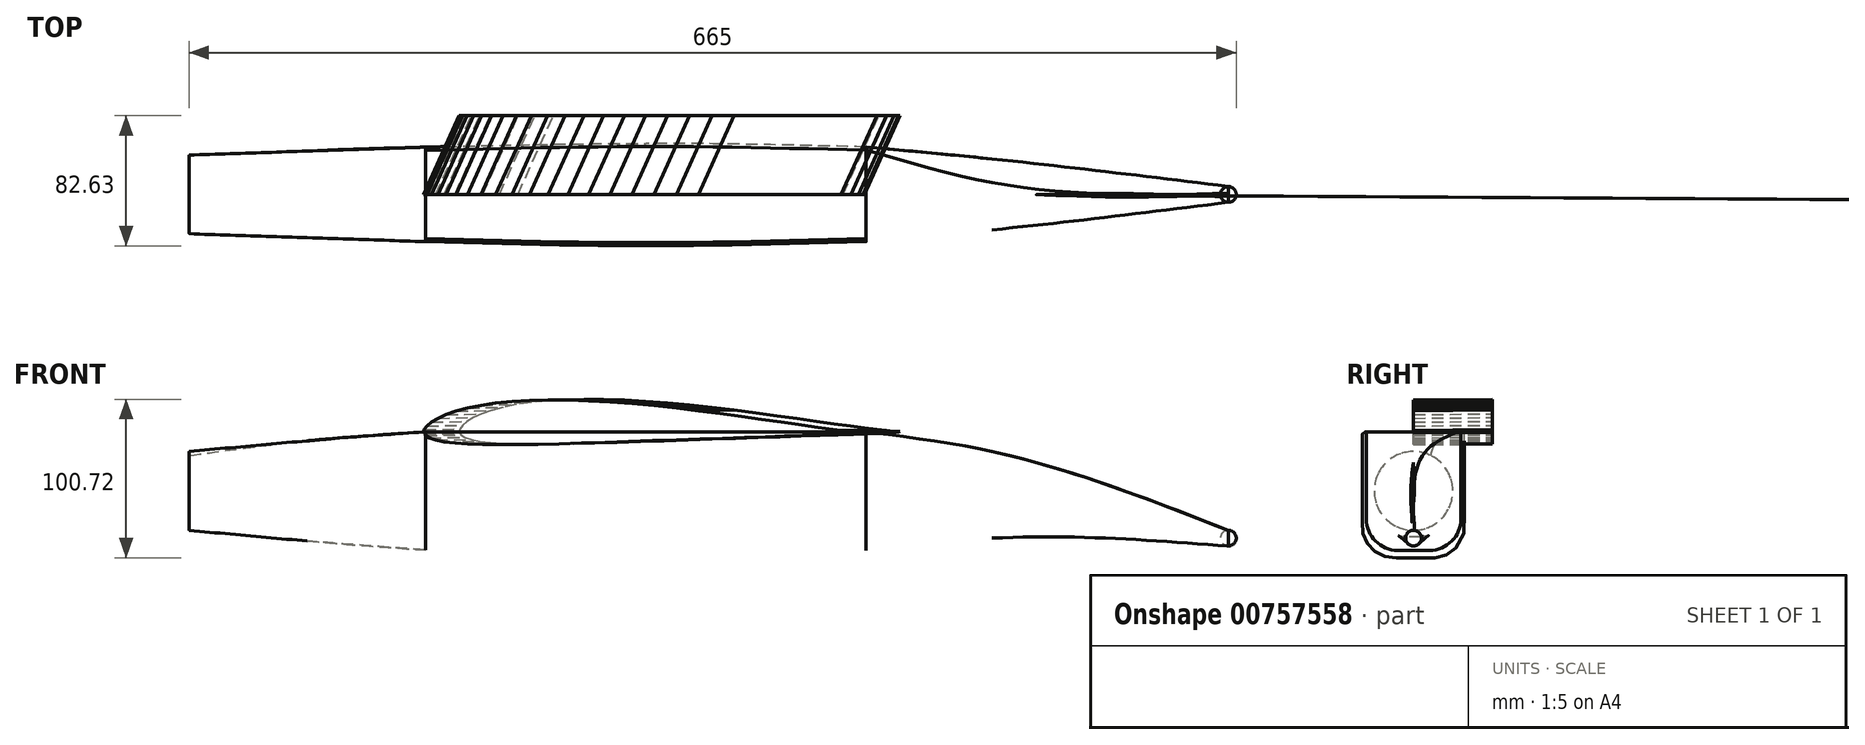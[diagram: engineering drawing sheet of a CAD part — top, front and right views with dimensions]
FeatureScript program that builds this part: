
annotation { "Feature Type Name" : "Feature", "Feature Type Description" : "" }
export const myFeature = defineFeature(function(context is Context, id is Id, definition is map)
    precondition{}
    {
        {
            var Q0;
            Q0=qCreatedBy(makeId("Right.planeOp"),FACE);
            cPlane(context, id + "F0", {"entities" : qUnion([Q0]), "cplaneType" : CPlaneType.OFFSET, "offset" : 150 * mm, "oppositeDirection" : true, "width" : 150 * mm, "height" : 150 * mm});
        }
        {
            var Q0;
            Q0=qCreatedBy(makeId("Right.planeOp"),FACE);
            cPlane(context, id + "F1", {"entities" : qUnion([Q0]), "cplaneType" : CPlaneType.OFFSET, "offset" : 280 * mm, "width" : 150 * mm, "height" : 150 * mm});
        }
        {
            var Q0;
            Q0=qCreatedBy(id+"F1.planeOp",FACE);
            cPlane(context, id + "F2", {"entities" : qUnion([Q0]), "cplaneType" : CPlaneType.OFFSET, "offset" : 230 * mm, "width" : 150 * mm, "height" : 150 * mm});
        }
        {
            var Q0;
            Q0=qCreatedBy(id+"F0.planeOp",FACE);
            var sketch = newSketch(context, id + "F3", { "sketchPlane" : qUnion([Q0])});
            skCircle(sketch, "E0", {"center": v(0, 0) * mm, "radius": 25 * mm});
            skSolve(sketch);
        }
        {
            var Q0;
            Q0=qCreatedBy(makeId("Right.planeOp"),FACE);
            var sketch = newSketch(context, id + "F4", { "sketchPlane" : qUnion([Q0])});
            skLineSegment(sketch, "E1.bottom", {"start": v(10, -37.5) * mm, "end": v(-10, -37.5) * mm});
            skLineSegment(sketch, "E1.top", {"start": v(28, 37.5) * mm, "end": v(-28, 37.5) * mm});
            skLineSegment(sketch, "E1.left", {"start": v(30, -17.5) * mm, "end": v(30, 35.5) * mm});
            skLineSegment(sketch, "E1.right", {"start": v(-30, -17.5) * mm, "end": v(-30, 35.5) * mm});
            skPoint(sketch, "E2.visualSharp", {"position": v(30, 37.5) * mm});
            skArc(sketch, "E2.filletArc", {"start": v(30, 35.5) * mm, "mid": v(29.41, 36.91) * mm, "end": v(28, 37.5) * mm});
            skPoint(sketch, "E3.visualSharp", {"position": v(-30, 37.5) * mm});
            skArc(sketch, "E3.filletArc", {"start": v(-28, 37.5) * mm, "mid": v(-29.41, 36.91) * mm, "end": v(-30, 35.5) * mm});
            skPoint(sketch, "E4.visualSharp", {"position": v(30, -37.5) * mm});
            skArc(sketch, "E4.filletArc", {"start": v(10, -37.5) * mm, "mid": v(24.14, -31.64) * mm, "end": v(30, -17.5) * mm});
            skPoint(sketch, "E5.visualSharp", {"position": v(-30, -37.5) * mm});
            skArc(sketch, "E5.filletArc", {"start": v(-30, -17.5) * mm, "mid": v(-24.14, -31.64) * mm, "end": v(-10, -37.5) * mm});
            skSolve(sketch);
        }
        {
            var Q0;
            Q0=qCreatedBy(id+"F1.planeOp",FACE);
            var sketch = newSketch(context, id + "F5", { "sketchPlane" : qUnion([Q0])});
            skLineSegment(sketch, "E6.bottom", {"start": v(28.14, 37.5) * mm, "end": v(-28, 37.5) * mm});
            skLineSegment(sketch, "E6.top", {"start": v(10.14, -37.77) * mm, "end": v(-10, -37.77) * mm});
            skLineSegment(sketch, "E6.left", {"start": v(30.14, 35.5) * mm, "end": v(30.14, -17.77) * mm});
            skLineSegment(sketch, "E6.right", {"start": v(-30, 35.5) * mm, "end": v(-30, -17.77) * mm});
            skPoint(sketch, "E7.visualSharp", {"position": v(30.14, -37.77) * mm});
            skArc(sketch, "E7.filletArc", {"start": v(10.14, -37.77) * mm, "mid": v(24.28, -31.9) * mm, "end": v(30.14, -17.77) * mm});
            skPoint(sketch, "E8.visualSharp", {"position": v(-30, -37.77) * mm});
            skArc(sketch, "E8.filletArc", {"start": v(-30, -17.77) * mm, "mid": v(-24.14, -31.9) * mm, "end": v(-10, -37.77) * mm});
            skPoint(sketch, "E9.visualSharp", {"position": v(30.14, 37.5) * mm});
            skArc(sketch, "E9.filletArc", {"start": v(30.14, 35.5) * mm, "mid": v(29.56, 36.91) * mm, "end": v(28.14, 37.5) * mm});
            skPoint(sketch, "E10.visualSharp", {"position": v(-30, 37.5) * mm});
            skArc(sketch, "E10.filletArc", {"start": v(-28, 37.5) * mm, "mid": v(-29.41, 36.91) * mm, "end": v(-30, 35.5) * mm});
            skSolve(sketch);
        }
        {
            var Q0;
            Q0=qCreatedBy(id+"F2.planeOp",FACE);
            var sketch = newSketch(context, id + "F6", { "sketchPlane" : qUnion([Q0])});
            skCircle(sketch, "E11", {"center": v(0, -30) * mm, "radius": 5 * mm});
            skSolve(sketch);
        }
        {
            var Q0;
            Q0=qCreatedBy(makeId("Right.planeOp"),FACE);
            cPlane(context, id + "F7", {"entities" : qUnion([Q0]), "cplaneType" : CPlaneType.OFFSET, "offset" : 75 * mm, "oppositeDirection" : true, "width" : 150 * mm, "height" : 150 * mm});
        }
        {
            var Q0;
            Q0=qCreatedBy(makeId("Right.planeOp"),FACE);
            cPlane(context, id + "F8", {"entities" : qUnion([Q0]), "cplaneType" : CPlaneType.OFFSET, "offset" : 140 * mm, "width" : 150 * mm, "height" : 150 * mm});
        }
        {
            var Q0;
            Q0=qCreatedBy(id+"F1.planeOp",FACE);
            cPlane(context, id + "F9", {"entities" : qUnion([Q0]), "cplaneType" : CPlaneType.OFFSET, "offset" : 80 * mm, "width" : 150 * mm, "height" : 150 * mm});
        }
        {
            var Q0;
            Q0=qCreatedBy(id+"F7.planeOp",FACE);
            var sketch = newSketch(context, id + "F10", { "sketchPlane" : qUnion([Q0])});
            skLineSegment(sketch, "E12.bottom", {"start": v(15.5, 31.79) * mm, "end": v(-15.5, 31.79) * mm});
            skLineSegment(sketch, "E12.top", {"start": v(5.5, -31.78) * mm, "end": v(-5.5, -31.78) * mm});
            skLineSegment(sketch, "E12.left", {"start": v(27.5, 19.79) * mm, "end": v(27.5, -9.78) * mm});
            skLineSegment(sketch, "E12.right", {"start": v(-27.5, 19.79) * mm, "end": v(-27.5, -9.78) * mm});
            skPoint(sketch, "E13.visualSharp", {"position": v(27.5, -31.78) * mm});
            skArc(sketch, "E13.filletArc", {"start": v(5.5, -31.78) * mm, "mid": v(21.06, -25.33) * mm, "end": v(27.5, -9.78) * mm});
            skPoint(sketch, "E14.visualSharp", {"position": v(-27.5, -31.78) * mm});
            skArc(sketch, "E14.filletArc", {"start": v(-27.5, -9.78) * mm, "mid": v(-21.06, -25.33) * mm, "end": v(-5.5, -31.78) * mm});
            skPoint(sketch, "E15.visualSharp", {"position": v(27.5, 31.79) * mm});
            skArc(sketch, "E15.filletArc", {"start": v(27.5, 19.79) * mm, "mid": v(23.99, 28.28) * mm, "end": v(15.5, 31.79) * mm});
            skPoint(sketch, "E16.visualSharp", {"position": v(-27.5, 31.79) * mm});
            skArc(sketch, "E16.filletArc", {"start": v(-15.5, 31.79) * mm, "mid": v(-23.99, 28.28) * mm, "end": v(-27.5, 19.79) * mm});
            skSolve(sketch);
        }
        {
            var Q0;
            Q0=qCreatedBy(id+"F8.planeOp",FACE);
            var sketch = newSketch(context, id + "F11", { "sketchPlane" : qUnion([Q0])});
            skLineSegment(sketch, "E17.bottom", {"start": v(30.37, 37.5) * mm, "end": v(-30.63, 37.5) * mm});
            skLineSegment(sketch, "E17.top", {"start": v(12.37, -42.5) * mm, "end": v(-12.63, -42.5) * mm});
            skLineSegment(sketch, "E17.left", {"start": v(32.37, 35.5) * mm, "end": v(32.37, -22.5) * mm});
            skLineSegment(sketch, "E17.right", {"start": v(-32.63, 35.5) * mm, "end": v(-32.63, -22.5) * mm});
            skPoint(sketch, "E18.visualSharp", {"position": v(32.37, -42.5) * mm});
            skArc(sketch, "E18.filletArc", {"start": v(12.37, -42.5) * mm, "mid": v(26.52, -36.64) * mm, "end": v(32.37, -22.5) * mm});
            skPoint(sketch, "E19.visualSharp", {"position": v(-32.63, -42.5) * mm});
            skArc(sketch, "E19.filletArc", {"start": v(-32.63, -22.5) * mm, "mid": v(-26.77, -36.64) * mm, "end": v(-12.63, -42.5) * mm});
            skPoint(sketch, "E20.visualSharp", {"position": v(32.37, 37.5) * mm});
            skArc(sketch, "E20.filletArc", {"start": v(32.37, 35.5) * mm, "mid": v(31.79, 36.91) * mm, "end": v(30.37, 37.5) * mm});
            skPoint(sketch, "E21.visualSharp", {"position": v(-32.63, 37.5) * mm});
            skArc(sketch, "E21.filletArc", {"start": v(-30.63, 37.5) * mm, "mid": v(-32.04, 36.91) * mm, "end": v(-32.63, 35.5) * mm});
            skSolve(sketch);
        }
        {
            var Q0;
            Q0=makeQuery(id+"F3.imprint","IMPRINT",FACE,{"disambiguationData":[TD([[makeQuery(id+"F3.imprint","IMPRINT",EDGE,{"derivedFrom":sQuery(id+"F3.wireOp",EDGE,"E0")}),1.0]])]});
            var Q1;
            Q1=makeQuery(id+"F10.imprint","IMPRINT",FACE,{"disambiguationData":[TD([[makeQuery(id+"F10.imprint","IMPRINT",EDGE,{"derivedFrom":sQuery(id+"F10.wireOp",EDGE,"E12.bottom")}),1.0]])]});
            var Q2;
            Q2=makeQuery(id+"F4.imprint","IMPRINT",FACE,{"disambiguationData":[TD([[makeQuery(id+"F4.imprint","IMPRINT",EDGE,{"derivedFrom":sQuery(id+"F4.wireOp",EDGE,"E1.bottom")}),-1.0]])]});
            loft(context, id + "F12", {"sheetProfilesArray" : [{ "sheetProfileEntities" : qUnion([Q0]) }, { "sheetProfileEntities" : qUnion([Q1]) }, { "sheetProfileEntities" : qUnion([Q2]) }]});
        }
        {
            var Q0;
            Q0=qCreatedBy(id+"F9.planeOp",FACE);
            var sketch = newSketch(context, id + "F13", { "sketchPlane" : qUnion([Q0])});
            skLineSegment(sketch, "E22.bottom", {"start": v(-7.5, 25) * mm, "end": v(7.5, 25) * mm});
            skLineSegment(sketch, "E22.top", {"start": v(-7.5, -30) * mm, "end": v(7.5, -30) * mm});
            skLineSegment(sketch, "E22.left", {"start": v(-22.5, 10) * mm, "end": v(-22.5, -15) * mm});
            skLineSegment(sketch, "E22.right", {"start": v(22.5, 10) * mm, "end": v(22.5, -15) * mm});
            skPoint(sketch, "E23.visualSharp", {"position": v(-22.5, 25) * mm});
            skArc(sketch, "E23.filletArc", {"start": v(-7.5, 25) * mm, "mid": v(-18.1, 20.6) * mm, "end": v(-22.5, 10) * mm});
            skPoint(sketch, "E24.visualSharp", {"position": v(22.5, 25) * mm});
            skArc(sketch, "E24.filletArc", {"start": v(22.5, 10) * mm, "mid": v(18.1, 20.6) * mm, "end": v(7.5, 25) * mm});
            skPoint(sketch, "E25.visualSharp", {"position": v(22.5, -30) * mm});
            skArc(sketch, "E25.filletArc", {"start": v(7.5, -30) * mm, "mid": v(18.1, -25.6) * mm, "end": v(22.5, -15) * mm});
            skPoint(sketch, "E26.visualSharp", {"position": v(-22.5, -30) * mm});
            skArc(sketch, "E26.filletArc", {"start": v(-22.5, -15) * mm, "mid": v(-18.1, -25.6) * mm, "end": v(-7.5, -30) * mm});
            skSolve(sketch);
        }
        {
            var Q0;
            Q0=makeQuery(id+"F5.imprint","IMPRINT",FACE,{"disambiguationData":[TD([[makeQuery(id+"F5.imprint","IMPRINT",EDGE,{"derivedFrom":sQuery(id+"F5.wireOp",EDGE,"E6.bottom")}),1.0]])]});
            var Q1;
            Q1=makeQuery(id+"F13.imprint","IMPRINT",FACE,{"disambiguationData":[TD([[makeQuery(id+"F13.imprint","IMPRINT",EDGE,{"derivedFrom":sQuery(id+"F13.wireOp",EDGE,"E22.bottom")}),-1.0]])]});
            var Q2;
            Q2=makeQuery(id+"F6.imprint","IMPRINT",FACE,{"disambiguationData":[TD([[makeQuery(id+"F6.imprint","IMPRINT",EDGE,{"derivedFrom":sQuery(id+"F6.wireOp",EDGE,"E11")}),1.0]])]});
            loft(context, id + "F14", {"sheetProfilesArray" : [{ "sheetProfileEntities" : qUnion([Q0]) }, { "sheetProfileEntities" : qUnion([Q1]) }, { "sheetProfileEntities" : qUnion([Q2]) }]});
        }
        {
            var Q0;
            Q0=makeQuery(id+"F12.opLoft","CAP_FACE",FACE,{"disambiguationData":[OSD([makeQuery(id+"F4.imprint","IMPRINT",FACE,{"disambiguationData":[TD([[makeQuery(id+"F4.imprint","IMPRINT",EDGE,{"derivedFrom":sQuery(id+"F4.wireOp",EDGE,"E1.bottom")}),-1.0]])]})])],"isStart":true});
            var Q1;
            Q1=makeQuery(id+"F11.imprint","IMPRINT",FACE,{"disambiguationData":[TD([[makeQuery(id+"F11.imprint","IMPRINT",EDGE,{"derivedFrom":sQuery(id+"F11.wireOp",EDGE,"E17.bottom")}),1.0]])]});
            var Q2;
            Q2=makeQuery(id+"F14.opLoft","CAP_FACE",FACE,{"disambiguationData":[OSD([makeQuery(id+"F5.imprint","IMPRINT",FACE,{"disambiguationData":[TD([[makeQuery(id+"F5.imprint","IMPRINT",EDGE,{"derivedFrom":sQuery(id+"F5.wireOp",EDGE,"E6.bottom")}),1.0]])]})])],"isStart":true});
            loft(context, id + "F15", {"sheetProfilesArray" : [{ "sheetProfileEntities" : qUnion([Q0]) }, { "sheetProfileEntities" : qUnion([Q1]) }, { "sheetProfileEntities" : qUnion([Q2]) }]});
        }
        {
            var Q0;
            Q0=qCreatedBy(id+"F2.planeOp",FACE);
            var sketch = newSketch(context, id + "F16", { "sketchPlane" : qUnion([Q0])});
            skCircle(sketch, "E27", {"center": v(0, -30) * mm, "radius": 5 * mm});
            skLineSegment(sketch, "E28", {"start": v(0, -45) * mm, "end": v(0, -15) * mm});
            skSolve(sketch);
        }
        {
            var Q0;
            {var subQ0=sQuery(id+"F16.wireOp",EDGE,"E28");var subQ1=sQuery(id+"F16.wireOp",EDGE,"E27");var subQ2=makeQuery(id+"F16.imprint","INTERSECT",VERTEX,{"disambiguationData":[OD(0.0)],"derivedFrom":[subQ1,subQ0]});Q0=makeQuery(id+"F16.imprint","IMPRINT",FACE,{"disambiguationData":[TD([[makeQuery(id+"F16.imprint","IMPRINT",EDGE,{"disambiguationData":[TD([[subQ2,1.0]])],"derivedFrom":subQ1}),1.0]])]});}
            var Q1;
            Q1=sQuery(id+"F16.wireOp",EDGE,"E27");
            var Q2;
            Q2=sQuery(id+"F16.wireOp",EDGE,"E28");
            revolve(context, id + "F17", {"surfaceOperationType" : NewSurfaceOperationType.NEW, "entities" : qUnion([Q0]), "surfaceEntities" : qUnion([Q1]), "axis" : qUnion([Q2]), "revolveType" : RevolveType.FULL});
        }
        {
            var Q0;
            Q0=qCreatedBy(makeId("Front.planeOp"),FACE);
            cPlane(context, id + "F18", {"entities" : qUnion([Q0]), "cplaneType" : CPlaneType.OFFSET, "offset" : 50 * mm, "width" : 150 * mm, "height" : 150 * mm});
        }
        {
            var Q0;
            Q0=qCreatedBy(makeId("Front.planeOp"),FACE);
            cPlane(context, id + "F19", {"entities" : qUnion([Q0]), "cplaneType" : CPlaneType.OFFSET, "offset" : 50 * mm, "oppositeDirection" : true, "width" : 150 * mm, "height" : 150 * mm});
        }
        {
            var Q0;
            Q0=qCreatedBy(makeId("Front.planeOp"),FACE);
            var sketch = newSketch(context, id + "F20", { "sketchPlane" : qUnion([Q0])});
            skLineSegment(sketch, "E29", {"start": v(278.84, 37.19) * mm, "end": v(277.87, 37.23) * mm});
            skLineSegment(sketch, "E30", {"start": v(277.87, 37.23) * mm, "end": v(275, 37.41) * mm});
            skLineSegment(sketch, "E31", {"start": v(275, 37.41) * mm, "end": v(270.35, 37.84) * mm});
            skLineSegment(sketch, "E32", {"start": v(270.35, 37.84) * mm, "end": v(264.1, 38.54) * mm});
            skLineSegment(sketch, "E33", {"start": v(264.1, 38.54) * mm, "end": v(256.35, 39.5) * mm});
            skLineSegment(sketch, "E34", {"start": v(256.35, 39.5) * mm, "end": v(247.27, 40.72) * mm});
            skLineSegment(sketch, "E35", {"start": v(247.27, 40.72) * mm, "end": v(237.01, 42.16) * mm});
            skLineSegment(sketch, "E36", {"start": v(237.01, 42.16) * mm, "end": v(225.73, 43.77) * mm});
            skLineSegment(sketch, "E37", {"start": v(225.73, 43.77) * mm, "end": v(213.58, 45.5) * mm});
            skLineSegment(sketch, "E38", {"start": v(213.58, 45.5) * mm, "end": v(200.7, 47.32) * mm});
            skLineSegment(sketch, "E39", {"start": v(200.7, 47.32) * mm, "end": v(187.3, 49.14) * mm});
            skLineSegment(sketch, "E40", {"start": v(187.3, 49.14) * mm, "end": v(173.48, 50.93) * mm});
            skLineSegment(sketch, "E41", {"start": v(173.48, 50.93) * mm, "end": v(159.43, 52.62) * mm});
            skLineSegment(sketch, "E42", {"start": v(159.43, 52.62) * mm, "end": v(145.3, 54.14) * mm});
            skLineSegment(sketch, "E43", {"start": v(145.3, 54.14) * mm, "end": v(131.22, 55.46) * mm});
            skLineSegment(sketch, "E44", {"start": v(131.22, 55.46) * mm, "end": v(117.33, 56.52) * mm});
            skLineSegment(sketch, "E45", {"start": v(117.33, 56.52) * mm, "end": v(103.77, 57.28) * mm});
            skLineSegment(sketch, "E46", {"start": v(103.77, 57.28) * mm, "end": v(90.65, 57.71) * mm});
            skLineSegment(sketch, "E47", {"start": v(90.65, 57.71) * mm, "end": v(78.09, 57.8) * mm});
            skLineSegment(sketch, "E48", {"start": v(78.09, 57.8) * mm, "end": v(66.2, 57.5) * mm});
            skLineSegment(sketch, "E49", {"start": v(66.2, 57.5) * mm, "end": v(55.05, 56.83) * mm});
            skLineSegment(sketch, "E50", {"start": v(55.05, 56.83) * mm, "end": v(44.74, 55.79) * mm});
            skLineSegment(sketch, "E51", {"start": v(44.74, 55.79) * mm, "end": v(35.34, 54.39) * mm});
            skLineSegment(sketch, "E52", {"start": v(35.34, 54.39) * mm, "end": v(26.9, 52.67) * mm});
            skLineSegment(sketch, "E53", {"start": v(26.9, 52.67) * mm, "end": v(19.5, 50.68) * mm});
            skLineSegment(sketch, "E54", {"start": v(19.5, 50.68) * mm, "end": v(13.15, 48.48) * mm});
            skLineSegment(sketch, "E55", {"start": v(13.15, 48.48) * mm, "end": v(7.93, 46.13) * mm});
            skLineSegment(sketch, "E56", {"start": v(7.93, 46.13) * mm, "end": v(3.87, 43.7) * mm});
            skLineSegment(sketch, "E57", {"start": v(3.87, 43.7) * mm, "end": v(1, 41.27) * mm});
            skLineSegment(sketch, "E58", {"start": v(1, 41.27) * mm, "end": v(-0.68, 38.93) * mm});
            skLineSegment(sketch, "E59", {"start": v(-0.68, 38.93) * mm, "end": v(-1.1, 37.72) * mm});
            skLineSegment(sketch, "E60", {"start": v(-1.1, 37.72) * mm, "end": v(-1.16, 37.22) * mm});
            skLineSegment(sketch, "E61", {"start": v(-1.16, 37.22) * mm, "end": v(-1.11, 36.78) * mm});
            skLineSegment(sketch, "E62", {"start": v(-1.11, 36.78) * mm, "end": v(-0.96, 36.36) * mm});
            skLineSegment(sketch, "E63", {"start": v(-0.96, 36.36) * mm, "end": v(-0.69, 35.94) * mm});
            skLineSegment(sketch, "E64", {"start": v(-0.69, 35.94) * mm, "end": v(0, 35.22) * mm});
            skLineSegment(sketch, "E65", {"start": v(0, 35.22) * mm, "end": v(2.6, 33.63) * mm});
            skLineSegment(sketch, "E66", {"start": v(2.6, 33.63) * mm, "end": v(6.61, 32.26) * mm});
            skLineSegment(sketch, "E67", {"start": v(6.61, 32.26) * mm, "end": v(12, 31.15) * mm});
            skLineSegment(sketch, "E68", {"start": v(12, 31.15) * mm, "end": v(18.78, 30.33) * mm});
            skLineSegment(sketch, "E69", {"start": v(18.78, 30.33) * mm, "end": v(26.93, 29.78) * mm});
            skLineSegment(sketch, "E70", {"start": v(26.93, 29.78) * mm, "end": v(36.36, 29.46) * mm});
            skLineSegment(sketch, "E71", {"start": v(36.36, 29.46) * mm, "end": v(47, 29.36) * mm});
            skLineSegment(sketch, "E72", {"start": v(47, 29.36) * mm, "end": v(58.76, 29.43) * mm});
            skLineSegment(sketch, "E73", {"start": v(58.76, 29.43) * mm, "end": v(71.48, 29.64) * mm});
            skLineSegment(sketch, "E74", {"start": v(71.48, 29.64) * mm, "end": v(85.03, 29.98) * mm});
            skLineSegment(sketch, "E75", {"start": v(85.03, 29.98) * mm, "end": v(99.25, 30.4) * mm});
            skLineSegment(sketch, "E76", {"start": v(99.25, 30.4) * mm, "end": v(113.98, 30.87) * mm});
            skLineSegment(sketch, "E77", {"start": v(113.98, 30.87) * mm, "end": v(129.03, 31.38) * mm});
            skLineSegment(sketch, "E78", {"start": v(129.03, 31.38) * mm, "end": v(144.22, 31.92) * mm});
            skLineSegment(sketch, "E79", {"start": v(144.22, 31.92) * mm, "end": v(159.37, 32.45) * mm});
            skLineSegment(sketch, "E80", {"start": v(159.37, 32.45) * mm, "end": v(174.3, 32.97) * mm});
            skLineSegment(sketch, "E81", {"start": v(174.3, 32.97) * mm, "end": v(188.81, 33.48) * mm});
            skLineSegment(sketch, "E82", {"start": v(188.81, 33.48) * mm, "end": v(202.75, 33.95) * mm});
            skLineSegment(sketch, "E83", {"start": v(202.75, 33.95) * mm, "end": v(215.93, 34.4) * mm});
            skLineSegment(sketch, "E84", {"start": v(215.93, 34.4) * mm, "end": v(228.2, 34.82) * mm});
            skLineSegment(sketch, "E85", {"start": v(228.2, 34.82) * mm, "end": v(239.41, 35.2) * mm});
            skLineSegment(sketch, "E86", {"start": v(239.41, 35.2) * mm, "end": v(249.42, 35.54) * mm});
            skLineSegment(sketch, "E87", {"start": v(249.42, 35.54) * mm, "end": v(258.1, 35.87) * mm});
            skLineSegment(sketch, "E88", {"start": v(258.1, 35.87) * mm, "end": v(265.36, 36.18) * mm});
            skLineSegment(sketch, "E89", {"start": v(265.36, 36.18) * mm, "end": v(271.1, 36.48) * mm});
            skLineSegment(sketch, "E90", {"start": v(271.1, 36.48) * mm, "end": v(275.28, 36.8) * mm});
            skLineSegment(sketch, "E91", {"start": v(275.28, 36.8) * mm, "end": v(277.91, 37.08) * mm});
            skLineSegment(sketch, "E92", {"start": v(277.91, 37.08) * mm, "end": v(278.84, 37.19) * mm});
            skSolve(sketch);
        }
        {
            var Q0;
            Q0=qCreatedBy(id+"F18.planeOp",FACE);
            var sketch = newSketch(context, id + "F21", { "sketchPlane" : qUnion([Q0])});
            skLineSegment(sketch, "E93", {"start": v(301.34, 37.61) * mm, "end": v(300.37, 37.65) * mm});
            skLineSegment(sketch, "E94", {"start": v(300.37, 37.65) * mm, "end": v(297.5, 37.84) * mm});
            skLineSegment(sketch, "E95", {"start": v(297.5, 37.84) * mm, "end": v(292.85, 38.27) * mm});
            skLineSegment(sketch, "E96", {"start": v(292.85, 38.27) * mm, "end": v(286.6, 38.96) * mm});
            skLineSegment(sketch, "E97", {"start": v(286.6, 38.96) * mm, "end": v(278.85, 39.93) * mm});
            skLineSegment(sketch, "E98", {"start": v(278.85, 39.93) * mm, "end": v(269.77, 41.15) * mm});
            skLineSegment(sketch, "E99", {"start": v(269.77, 41.15) * mm, "end": v(259.51, 42.58) * mm});
            skLineSegment(sketch, "E100", {"start": v(259.51, 42.58) * mm, "end": v(248.23, 44.2) * mm});
            skLineSegment(sketch, "E101", {"start": v(248.23, 44.2) * mm, "end": v(236.08, 45.93) * mm});
            skLineSegment(sketch, "E102", {"start": v(236.08, 45.93) * mm, "end": v(223.2, 47.74) * mm});
            skLineSegment(sketch, "E103", {"start": v(223.2, 47.74) * mm, "end": v(209.8, 49.57) * mm});
            skLineSegment(sketch, "E104", {"start": v(209.8, 49.57) * mm, "end": v(195.98, 51.36) * mm});
            skLineSegment(sketch, "E105", {"start": v(195.98, 51.36) * mm, "end": v(181.93, 53.04) * mm});
            skLineSegment(sketch, "E106", {"start": v(181.93, 53.04) * mm, "end": v(167.8, 54.57) * mm});
            skLineSegment(sketch, "E107", {"start": v(167.8, 54.57) * mm, "end": v(153.72, 55.88) * mm});
            skLineSegment(sketch, "E108", {"start": v(153.72, 55.88) * mm, "end": v(139.83, 56.95) * mm});
            skLineSegment(sketch, "E109", {"start": v(139.83, 56.95) * mm, "end": v(126.27, 57.7) * mm});
            skLineSegment(sketch, "E110", {"start": v(126.27, 57.7) * mm, "end": v(113.15, 58.14) * mm});
            skLineSegment(sketch, "E111", {"start": v(113.15, 58.14) * mm, "end": v(100.59, 58.22) * mm});
            skLineSegment(sketch, "E112", {"start": v(100.59, 58.22) * mm, "end": v(88.7, 57.92) * mm});
            skLineSegment(sketch, "E113", {"start": v(88.7, 57.92) * mm, "end": v(77.55, 57.25) * mm});
            skLineSegment(sketch, "E114", {"start": v(77.55, 57.25) * mm, "end": v(67.24, 56.21) * mm});
            skLineSegment(sketch, "E115", {"start": v(67.24, 56.21) * mm, "end": v(57.84, 54.81) * mm});
            skLineSegment(sketch, "E116", {"start": v(57.84, 54.81) * mm, "end": v(49.4, 53.1) * mm});
            skLineSegment(sketch, "E117", {"start": v(49.4, 53.1) * mm, "end": v(42, 51.11) * mm});
            skLineSegment(sketch, "E118", {"start": v(42, 51.11) * mm, "end": v(35.65, 48.9) * mm});
            skLineSegment(sketch, "E119", {"start": v(35.65, 48.9) * mm, "end": v(30.43, 46.56) * mm});
            skLineSegment(sketch, "E120", {"start": v(30.43, 46.56) * mm, "end": v(26.37, 44.12) * mm});
            skLineSegment(sketch, "E121", {"start": v(26.37, 44.12) * mm, "end": v(23.5, 41.7) * mm});
            skLineSegment(sketch, "E122", {"start": v(23.5, 41.7) * mm, "end": v(21.82, 39.36) * mm});
            skLineSegment(sketch, "E123", {"start": v(21.82, 39.36) * mm, "end": v(21.4, 38.14) * mm});
            skLineSegment(sketch, "E124", {"start": v(21.4, 38.14) * mm, "end": v(21.34, 37.65) * mm});
            skLineSegment(sketch, "E125", {"start": v(21.34, 37.65) * mm, "end": v(21.39, 37.2) * mm});
            skLineSegment(sketch, "E126", {"start": v(21.39, 37.2) * mm, "end": v(21.54, 36.79) * mm});
            skLineSegment(sketch, "E127", {"start": v(21.54, 36.79) * mm, "end": v(21.81, 36.37) * mm});
            skLineSegment(sketch, "E128", {"start": v(21.81, 36.37) * mm, "end": v(22.5, 35.64) * mm});
            skLineSegment(sketch, "E129", {"start": v(22.5, 35.64) * mm, "end": v(25.1, 34.06) * mm});
            skLineSegment(sketch, "E130", {"start": v(25.1, 34.06) * mm, "end": v(29.11, 32.68) * mm});
            skLineSegment(sketch, "E131", {"start": v(29.11, 32.68) * mm, "end": v(34.5, 31.58) * mm});
            skLineSegment(sketch, "E132", {"start": v(34.5, 31.58) * mm, "end": v(41.28, 30.76) * mm});
            skLineSegment(sketch, "E133", {"start": v(41.28, 30.76) * mm, "end": v(49.43, 30.2) * mm});
            skLineSegment(sketch, "E134", {"start": v(49.43, 30.2) * mm, "end": v(58.86, 29.89) * mm});
            skLineSegment(sketch, "E135", {"start": v(58.86, 29.89) * mm, "end": v(69.5, 29.78) * mm});
            skLineSegment(sketch, "E136", {"start": v(69.5, 29.78) * mm, "end": v(81.26, 29.86) * mm});
            skLineSegment(sketch, "E137", {"start": v(81.26, 29.86) * mm, "end": v(93.98, 30.07) * mm});
            skLineSegment(sketch, "E138", {"start": v(93.98, 30.07) * mm, "end": v(107.53, 30.4) * mm});
            skLineSegment(sketch, "E139", {"start": v(107.53, 30.4) * mm, "end": v(121.75, 30.82) * mm});
            skLineSegment(sketch, "E140", {"start": v(121.75, 30.82) * mm, "end": v(136.48, 31.3) * mm});
            skLineSegment(sketch, "E141", {"start": v(136.48, 31.3) * mm, "end": v(151.53, 31.81) * mm});
            skLineSegment(sketch, "E142", {"start": v(151.53, 31.81) * mm, "end": v(166.72, 32.34) * mm});
            skLineSegment(sketch, "E143", {"start": v(166.72, 32.34) * mm, "end": v(181.87, 32.88) * mm});
            skLineSegment(sketch, "E144", {"start": v(181.87, 32.88) * mm, "end": v(196.8, 33.4) * mm});
            skLineSegment(sketch, "E145", {"start": v(196.8, 33.4) * mm, "end": v(211.31, 33.9) * mm});
            skLineSegment(sketch, "E146", {"start": v(211.31, 33.9) * mm, "end": v(225.25, 34.38) * mm});
            skLineSegment(sketch, "E147", {"start": v(225.25, 34.38) * mm, "end": v(238.43, 34.83) * mm});
            skLineSegment(sketch, "E148", {"start": v(238.43, 34.83) * mm, "end": v(250.7, 35.24) * mm});
            skLineSegment(sketch, "E149", {"start": v(250.7, 35.24) * mm, "end": v(261.91, 35.62) * mm});
            skLineSegment(sketch, "E150", {"start": v(261.91, 35.62) * mm, "end": v(271.92, 35.97) * mm});
            skLineSegment(sketch, "E151", {"start": v(271.92, 35.97) * mm, "end": v(280.6, 36.3) * mm});
            skLineSegment(sketch, "E152", {"start": v(280.6, 36.3) * mm, "end": v(287.86, 36.6) * mm});
            skLineSegment(sketch, "E153", {"start": v(287.86, 36.6) * mm, "end": v(293.6, 36.9) * mm});
            skLineSegment(sketch, "E154", {"start": v(293.6, 36.9) * mm, "end": v(297.78, 37.23) * mm});
            skLineSegment(sketch, "E155", {"start": v(297.78, 37.23) * mm, "end": v(300.41, 37.5) * mm});
            skLineSegment(sketch, "E156", {"start": v(300.41, 37.5) * mm, "end": v(301.34, 37.61) * mm});
            skSolve(sketch);
        }
        {
            var Q0;
            Q0=qCreatedBy(id+"F19.planeOp",FACE);
            var sketch = newSketch(context, id + "F22", { "sketchPlane" : qUnion([Q0])});
            skLineSegment(sketch, "E157", {"start": v(301.43, 37.61) * mm, "end": v(300.46, 37.65) * mm});
            skLineSegment(sketch, "E158", {"start": v(300.46, 37.65) * mm, "end": v(297.58, 37.84) * mm});
            skLineSegment(sketch, "E159", {"start": v(297.58, 37.84) * mm, "end": v(292.95, 38.27) * mm});
            skLineSegment(sketch, "E160", {"start": v(292.95, 38.27) * mm, "end": v(286.68, 38.96) * mm});
            skLineSegment(sketch, "E161", {"start": v(286.68, 38.96) * mm, "end": v(278.94, 39.93) * mm});
            skLineSegment(sketch, "E162", {"start": v(278.94, 39.93) * mm, "end": v(269.86, 41.15) * mm});
            skLineSegment(sketch, "E163", {"start": v(269.86, 41.15) * mm, "end": v(259.6, 42.58) * mm});
            skLineSegment(sketch, "E164", {"start": v(259.6, 42.58) * mm, "end": v(248.32, 44.2) * mm});
            skLineSegment(sketch, "E165", {"start": v(248.32, 44.2) * mm, "end": v(236.17, 45.93) * mm});
            skLineSegment(sketch, "E166", {"start": v(236.17, 45.93) * mm, "end": v(223.3, 47.74) * mm});
            skLineSegment(sketch, "E167", {"start": v(223.3, 47.74) * mm, "end": v(209.88, 49.57) * mm});
            skLineSegment(sketch, "E168", {"start": v(209.88, 49.57) * mm, "end": v(196.07, 51.36) * mm});
            skLineSegment(sketch, "E169", {"start": v(196.07, 51.36) * mm, "end": v(182.03, 53.04) * mm});
            skLineSegment(sketch, "E170", {"start": v(182.03, 53.04) * mm, "end": v(167.9, 54.57) * mm});
            skLineSegment(sketch, "E171", {"start": v(167.9, 54.57) * mm, "end": v(153.81, 55.88) * mm});
            skLineSegment(sketch, "E172", {"start": v(153.81, 55.88) * mm, "end": v(139.93, 56.95) * mm});
            skLineSegment(sketch, "E173", {"start": v(139.93, 56.95) * mm, "end": v(126.36, 57.7) * mm});
            skLineSegment(sketch, "E174", {"start": v(126.36, 57.7) * mm, "end": v(113.24, 58.14) * mm});
            skLineSegment(sketch, "E175", {"start": v(113.24, 58.14) * mm, "end": v(100.68, 58.22) * mm});
            skLineSegment(sketch, "E176", {"start": v(100.68, 58.22) * mm, "end": v(88.78, 57.92) * mm});
            skLineSegment(sketch, "E177", {"start": v(88.78, 57.92) * mm, "end": v(77.64, 57.25) * mm});
            skLineSegment(sketch, "E178", {"start": v(77.64, 57.25) * mm, "end": v(67.33, 56.21) * mm});
            skLineSegment(sketch, "E179", {"start": v(67.33, 56.21) * mm, "end": v(57.93, 54.81) * mm});
            skLineSegment(sketch, "E180", {"start": v(57.93, 54.81) * mm, "end": v(49.5, 53.1) * mm});
            skLineSegment(sketch, "E181", {"start": v(49.5, 53.1) * mm, "end": v(42.08, 51.11) * mm});
            skLineSegment(sketch, "E182", {"start": v(42.08, 51.11) * mm, "end": v(35.74, 48.9) * mm});
            skLineSegment(sketch, "E183", {"start": v(35.74, 48.9) * mm, "end": v(30.52, 46.56) * mm});
            skLineSegment(sketch, "E184", {"start": v(30.52, 46.56) * mm, "end": v(26.46, 44.12) * mm});
            skLineSegment(sketch, "E185", {"start": v(26.46, 44.12) * mm, "end": v(23.59, 41.7) * mm});
            skLineSegment(sketch, "E186", {"start": v(23.59, 41.7) * mm, "end": v(21.9, 39.36) * mm});
            skLineSegment(sketch, "E187", {"start": v(21.9, 39.36) * mm, "end": v(21.5, 38.14) * mm});
            skLineSegment(sketch, "E188", {"start": v(21.5, 38.14) * mm, "end": v(21.43, 37.65) * mm});
            skLineSegment(sketch, "E189", {"start": v(21.43, 37.65) * mm, "end": v(21.48, 37.2) * mm});
            skLineSegment(sketch, "E190", {"start": v(21.48, 37.2) * mm, "end": v(21.63, 36.79) * mm});
            skLineSegment(sketch, "E191", {"start": v(21.63, 36.79) * mm, "end": v(21.9, 36.37) * mm});
            skLineSegment(sketch, "E192", {"start": v(21.9, 36.37) * mm, "end": v(22.6, 35.64) * mm});
            skLineSegment(sketch, "E193", {"start": v(22.6, 35.64) * mm, "end": v(25.2, 34.06) * mm});
            skLineSegment(sketch, "E194", {"start": v(25.2, 34.06) * mm, "end": v(29.2, 32.68) * mm});
            skLineSegment(sketch, "E195", {"start": v(29.2, 32.68) * mm, "end": v(34.6, 31.58) * mm});
            skLineSegment(sketch, "E196", {"start": v(34.6, 31.58) * mm, "end": v(41.37, 30.76) * mm});
            skLineSegment(sketch, "E197", {"start": v(41.37, 30.76) * mm, "end": v(49.52, 30.2) * mm});
            skLineSegment(sketch, "E198", {"start": v(49.52, 30.2) * mm, "end": v(58.95, 29.89) * mm});
            skLineSegment(sketch, "E199", {"start": v(58.95, 29.89) * mm, "end": v(69.6, 29.78) * mm});
            skLineSegment(sketch, "E200", {"start": v(69.6, 29.78) * mm, "end": v(81.35, 29.86) * mm});
            skLineSegment(sketch, "E201", {"start": v(81.35, 29.86) * mm, "end": v(94.07, 30.07) * mm});
            skLineSegment(sketch, "E202", {"start": v(94.07, 30.07) * mm, "end": v(107.62, 30.4) * mm});
            skLineSegment(sketch, "E203", {"start": v(107.62, 30.4) * mm, "end": v(121.85, 30.82) * mm});
            skLineSegment(sketch, "E204", {"start": v(121.85, 30.82) * mm, "end": v(136.57, 31.3) * mm});
            skLineSegment(sketch, "E205", {"start": v(136.57, 31.3) * mm, "end": v(151.62, 31.81) * mm});
            skLineSegment(sketch, "E206", {"start": v(151.62, 31.81) * mm, "end": v(166.81, 32.34) * mm});
            skLineSegment(sketch, "E207", {"start": v(166.81, 32.34) * mm, "end": v(181.96, 32.88) * mm});
            skLineSegment(sketch, "E208", {"start": v(181.96, 32.88) * mm, "end": v(196.89, 33.4) * mm});
            skLineSegment(sketch, "E209", {"start": v(196.89, 33.4) * mm, "end": v(211.4, 33.9) * mm});
            skLineSegment(sketch, "E210", {"start": v(211.4, 33.9) * mm, "end": v(225.34, 34.38) * mm});
            skLineSegment(sketch, "E211", {"start": v(225.34, 34.38) * mm, "end": v(238.52, 34.83) * mm});
            skLineSegment(sketch, "E212", {"start": v(238.52, 34.83) * mm, "end": v(250.8, 35.24) * mm});
            skLineSegment(sketch, "E213", {"start": v(250.8, 35.24) * mm, "end": v(262, 35.62) * mm});
            skLineSegment(sketch, "E214", {"start": v(262, 35.62) * mm, "end": v(272, 35.97) * mm});
            skLineSegment(sketch, "E215", {"start": v(272, 35.97) * mm, "end": v(280.7, 36.3) * mm});
            skLineSegment(sketch, "E216", {"start": v(280.7, 36.3) * mm, "end": v(287.95, 36.6) * mm});
            skLineSegment(sketch, "E217", {"start": v(287.95, 36.6) * mm, "end": v(293.69, 36.9) * mm});
            skLineSegment(sketch, "E218", {"start": v(293.69, 36.9) * mm, "end": v(297.87, 37.23) * mm});
            skLineSegment(sketch, "E219", {"start": v(297.87, 37.23) * mm, "end": v(300.5, 37.5) * mm});
            skLineSegment(sketch, "E220", {"start": v(300.5, 37.5) * mm, "end": v(301.43, 37.61) * mm});
            skSolve(sketch);
        }
        {
            var Q0;
            Q0=makeQuery(id+"F20.imprint","IMPRINT",FACE,{"disambiguationData":[TD([[makeQuery(id+"F20.imprint","IMPRINT",EDGE,{"derivedFrom":sQuery(id+"F20.wireOp",EDGE,"E29")}),1.0]])]});
            var Q1;
            Q1=makeQuery(id+"F22.imprint","IMPRINT",FACE,{"disambiguationData":[TD([[makeQuery(id+"F22.imprint","IMPRINT",EDGE,{"derivedFrom":sQuery(id+"F22.wireOp",EDGE,"E157")}),1.0]])]});
            loft(context, id + "F23", {"sheetProfilesArray" : [{ "sheetProfileEntities" : qUnion([Q0]) }, { "sheetProfileEntities" : qUnion([Q1]) }]});
        }
        {
            var Q0;
            Q0=makeQuery(id+"F23.opLoft","CAP_FACE",FACE,{"disambiguationData":[OSD([makeQuery(id+"F20.imprint","IMPRINT",FACE,{"disambiguationData":[TD([[makeQuery(id+"F20.imprint","IMPRINT",EDGE,{"derivedFrom":sQuery(id+"F20.wireOp",EDGE,"E29")}),1.0]])]})])],"isStart":true});
            var Q1;
            Q1=makeQuery(id+"F21.imprint","IMPRINT",FACE,{"disambiguationData":[TD([[makeQuery(id+"F21.imprint","IMPRINT",EDGE,{"derivedFrom":sQuery(id+"F21.wireOp",EDGE,"E93")}),1.0]])]});
            loft(context, id + "F24", {"sheetProfilesArray" : [{ "sheetProfileEntities" : qUnion([Q0]) }, { "sheetProfileEntities" : qUnion([Q1]) }]});
        }
        {
            var Q0;
            Q0=makeQuery(id+"F24.opLoft","SWEPT_BODY",BODY,{"disambiguationData":[OSD([makeQuery(id+"F20.imprint","IMPRINT",FACE,{"disambiguationData":[TD([[makeQuery(id+"F20.imprint","IMPRINT",EDGE,{"derivedFrom":sQuery(id+"F20.wireOp",EDGE,"E29")}),1.0]])]}),makeQuery(id+"F21.imprint","IMPRINT",FACE,{"disambiguationData":[TD([[makeQuery(id+"F21.imprint","IMPRINT",EDGE,{"derivedFrom":sQuery(id+"F21.wireOp",EDGE,"E93")}),1.0]])]})])]});
            var Q1;
            Q1=makeQuery(id+"F17.opRevolve","SWEPT_BODY",BODY,{"disambiguationData":[OSD([sQuery(id+"F16.wireOp",EDGE,"E27"),sQuery(id+"F16.wireOp",EDGE,"E28")])]});
            booleanBodies(context, id + "F25", {"operationType" : BooleanOperationType.SUBTRACTION, "tools" : qUnion([Q0]), "targets" : qUnion([Q1])});
        }
    });
